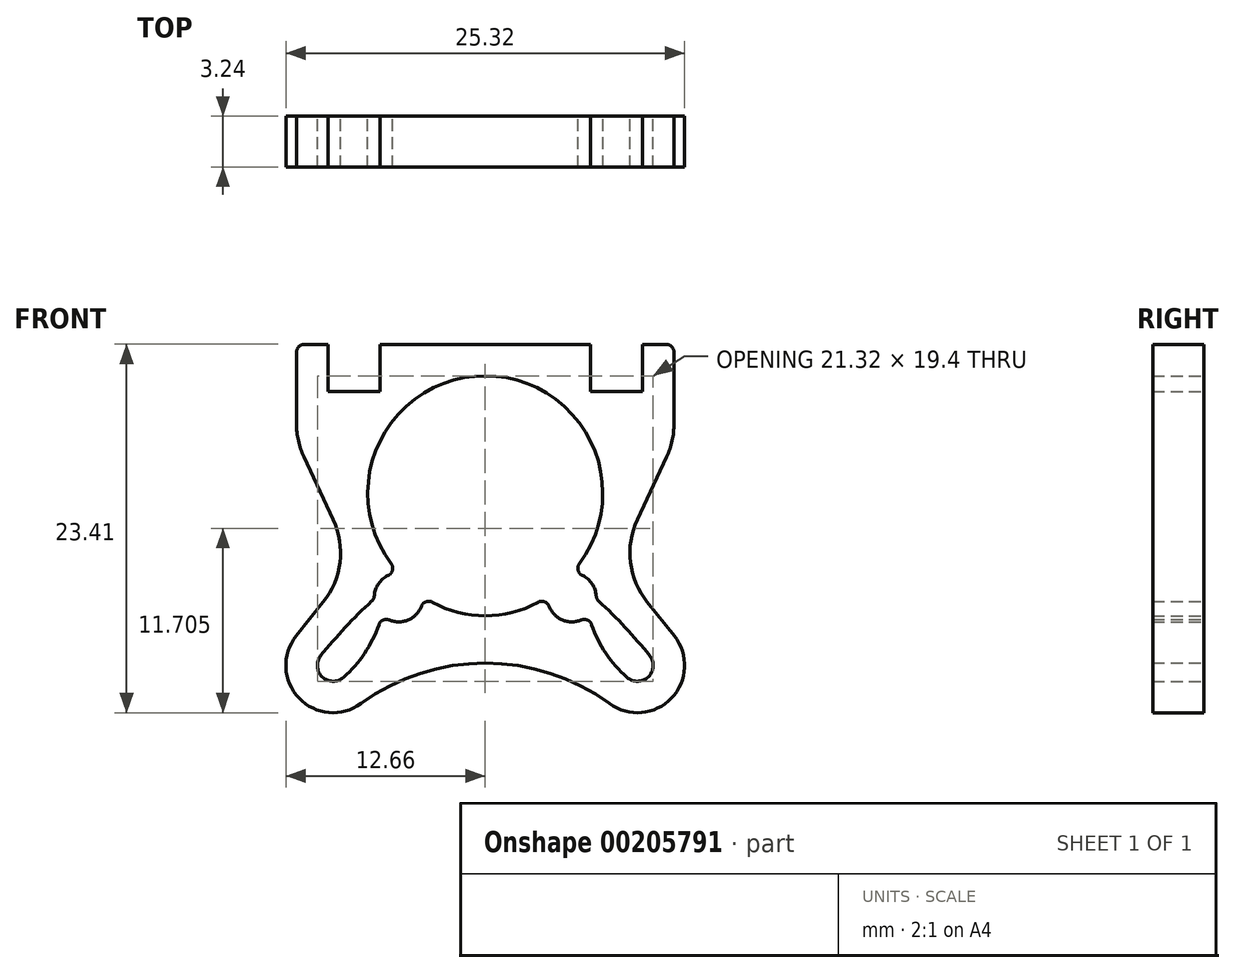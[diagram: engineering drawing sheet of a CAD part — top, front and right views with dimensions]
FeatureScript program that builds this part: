
annotation { "Feature Type Name" : "Feature", "Feature Type Description" : "" }
export const myFeature = defineFeature(function(context is Context, id is Id, definition is map)
    precondition{}
    {
        {
            var Q0;
            Q0=qCreatedBy(makeId("Front.planeOp"),FACE);
            var sketch = newSketch(context, id + "F0", { "sketchPlane" : qUnion([Q0])});
            skCircle(sketch, "E0", {"center": v(0, 0) * mm, "radius": 6.38 * mm});
            skPoint(sketch, "E1", {"position": v(0, 6.38) * mm});
            skPoint(sketch, "E2", {"position": v(0, 11.38) * mm});
            skCircle(sketch, "E3", {"center": v(-5.5, -5.7) * mm, "radius": 1.55 * mm});
            skLineSegment(sketch, "E4", {"start": v(0, 11.38) * mm, "end": v(0, 0) * mm, "construction": true});
            skCircle(sketch, "E5.MirrorC", {"center": v(5.5, -5.7) * mm, "radius": 1.55 * mm});
            skLineSegment(sketch, "E6", {"start": v(-5.5, -5.7) * mm, "end": v(5.5, -5.7) * mm, "construction": true});
            skSolve(sketch);
        }
        {
            var Q0;
            Q0=qCreatedBy(makeId("Front.planeOp"),FACE);
            var sketch = newSketch(context, id + "F1", { "sketchPlane" : qUnion([Q0])});
            skArc(sketch, "E7.0", {"start": v(-3.95, -5.63) * mm, "mid": v(-2.07, -6.56) * mm, "end": v(0, -6.88) * mm});
            skArc(sketch, "E8.3", {"start": v(-6.58, -6.82) * mm, "mid": v(-4.86, -7.12) * mm, "end": v(-3.95, -5.63) * mm});
            skLineSegment(sketch, "E9", {"start": v(0, 0) * mm, "end": v(-9.66, -10.03) * mm, "construction": true});
            skArc(sketch, "E10", {"start": v(-10.44, -9.4) * mm, "mid": v(-10.36, -10.75) * mm, "end": v(-9, -10.78) * mm});
            skLineSegment(sketch, "E11", {"start": v(-5.48, -4.16) * mm, "end": v(-7.05, -5.79) * mm, "construction": true});
            skLineSegment(sketch, "E12", {"start": v(-3.95, -5.63) * mm, "end": v(-5.52, -7.26) * mm, "construction": true});
            skLineSegment(sketch, "E13", {"start": v(-9, -10.78) * mm, "end": v(-4.74, -7.06) * mm, "construction": true});
            skPoint(sketch, "E13.endSnap0", {"position": v(-4.74, -6.44) * mm});
            skLineSegment(sketch, "E14", {"start": v(-6.7, -4.74) * mm, "end": v(-10.44, -9.4) * mm, "construction": true});
            skArc(sketch, "E15.trimOffspring", {"start": v(-12, -8.15) * mm, "mid": v(-11.83, -12.1) * mm, "end": v(-7.9, -12.45) * mm});
            skLineSegment(sketch, "E16", {"start": v(0, 0) * mm, "end": v(0, -9.88) * mm, "construction": true});
            skArc(sketch, "E17", {"start": v(0, -9.88) * mm, "mid": v(-4.15, -10.53) * mm, "end": v(-7.9, -12.45) * mm});
            skLineSegment(sketch, "E18", {"start": v(0, -9.88) * mm, "end": v(-5.5, -9.88) * mm, "construction": true});
            skLineSegment(sketch, "E19", {"start": v(0, -9.88) * mm, "end": v(0, -6.88) * mm});
            skArc(sketch, "E20", {"start": v(-5.48, -4.16) * mm, "mid": v(-6.62, -4.63) * mm, "end": v(-7.05, -5.79) * mm});
            skArc(sketch, "E21", {"start": v(-7.05, -5.79) * mm, "mid": v(-8.82, -7.53) * mm, "end": v(-10.44, -9.4) * mm});
            skLineSegment(sketch, "E22", {"start": v(-12, -8.15) * mm, "end": v(-8.33, -3.57) * mm});
            skArc(sketch, "E23", {"start": v(0, 8.37) * mm, "mid": v(-6.84, 3.9) * mm, "end": v(-5.48, -4.16) * mm});
            skLineSegment(sketch, "E24", {"start": v(0, 8.38) * mm, "end": v(0, 10.37) * mm});
            skLineSegment(sketch, "E25", {"start": v(-11.99, 4.22) * mm, "end": v(-8.57, -3.09) * mm});
            skArc(sketch, "E26.trimOffspring", {"start": v(-8.57, -3.09) * mm, "mid": v(-8.46, -3.33) * mm, "end": v(-8.33, -3.57) * mm});
            skArc(sketch, "E27", {"start": v(-9, -10.78) * mm, "mid": v(-7.49, -8.99) * mm, "end": v(-6.58, -6.82) * mm});
            skLineSegment(sketch, "E28", {"start": v(0, 10.37) * mm, "end": v(-6.69, 10.37) * mm});
            skLineSegment(sketch, "E29", {"start": v(-6.69, 10.37) * mm, "end": v(-6.69, 7.37) * mm});
            skLineSegment(sketch, "E30", {"start": v(-6.69, 7.37) * mm, "end": v(-9.99, 7.37) * mm});
            skLineSegment(sketch, "E31", {"start": v(-9.99, 7.37) * mm, "end": v(-9.99, 10.37) * mm});
            skLineSegment(sketch, "E32", {"start": v(-9.99, 10.37) * mm, "end": v(-11.99, 10.37) * mm});
            skLineSegment(sketch, "E33", {"start": v(-11.99, 10.37) * mm, "end": v(-11.99, 4.22) * mm});
            skLineSegment(sketch, "E34", {"start": v(-9.99, 10.37) * mm, "end": v(-9.99, 4.22) * mm, "construction": true});
            skLineSegment(sketch, "E35", {"start": v(-9.99, 4.22) * mm, "end": v(-6.69, 4.22) * mm, "construction": true});
            skLineSegment(sketch, "E36", {"start": v(-6.69, 4.22) * mm, "end": v(-6.69, 10.37) * mm, "construction": true});
            skLineSegment(sketch, "E37", {"start": v(-9.66, -13.03) * mm, "end": v(0, -13.03) * mm, "construction": true});
            skLineSegment(sketch, "E38", {"start": v(0, -13.03) * mm, "end": v(0, -6.88) * mm, "construction": true});
            skSolve(sketch);
        }
        {
            var Q0;
            Q0=qSketchRegion(id+"F1",true);
            extrude(context, id + "F2", {"entities" : qUnion([Q0]), "depth" : 3.25 * mm, "symmetric" : true});
        }
        {
            var Q0;
            Q0=makeQuery(id+"F2.opExtrude","SWEPT_EDGE",EDGE,{"disambiguationData":[OSD([sQuery(id+"F1.wireOp",EDGE,"E8.3"),sQuery(id+"F1.wireOp",EDGE,"f16a48b5-7a2a-4cbf-833e-9f4b7a7ec827.trimOffspring")])]});
            var Q1;
            Q1=makeQuery(id+"F2.opExtrude","SWEPT_EDGE",EDGE,{"disambiguationData":[OSD([sQuery(id+"F1.wireOp",EDGE,"0503ed2f-4905-41a0-8b90-6c5d83e06de4"),sQuery(id+"F1.wireOp",EDGE,"E8.3")])]});
            var Q2;
            Q2=makeQuery(id+"F2.opExtrude","SWEPT_EDGE",EDGE,{"disambiguationData":[OSD([sQuery(id+"F1.wireOp",EDGE,"E7.0"),sQuery(id+"F1.wireOp",EDGE,"E8.3")])]});
            var Q3;
            Q3=makeQuery(id+"F2.opExtrude","SWEPT_EDGE",EDGE,{"disambiguationData":[OSD([sQuery(id+"F1.wireOp",EDGE,"E20"),sQuery(id+"F1.wireOp",EDGE,"E21")])]});
            var Q4;
            Q4=makeQuery(id+"F2.opExtrude","SWEPT_EDGE",EDGE,{"disambiguationData":[OSD([sQuery(id+"F1.wireOp",EDGE,"E20"),sQuery(id+"F1.wireOp",EDGE,"aa0188ab-c223-4f96-b803-20454a8c8853")])]});
            var Q5;
            Q5=makeQuery(id+"F2.opExtrude","SWEPT_EDGE",EDGE,{"disambiguationData":[OSD([sQuery(id+"F1.wireOp",EDGE,"e83e305f-1027-4866-97f5-19716599f6f7"),sQuery(id+"F1.wireOp",EDGE,"E8.3")])]});
            var Q6;
            Q6=makeQuery(id+"F2.opExtrude","SWEPT_EDGE",EDGE,{"disambiguationData":[OSD([sQuery(id+"F1.wireOp",EDGE,"E10"),sQuery(id+"F1.wireOp",EDGE,"e83e305f-1027-4866-97f5-19716599f6f7")])]});
            var Q7;
            Q7=makeQuery(id+"F2.opExtrude","SWEPT_EDGE",EDGE,{"disambiguationData":[OSD([sQuery(id+"F1.wireOp",EDGE,"E32"),sQuery(id+"F1.wireOp",EDGE,"E33")])]});
            fillet(context, id + "F3", {"entities" : qUnion([Q0, Q1, Q2, Q3, Q4, Q5, Q6, Q7]), "radius" : 0.5 * mm, "tangentPropagation" : true, "allowEdgeOverflow" : false});
        }
        {
            var Q0;
            Q0=makeQuery(id+"F2.opExtrude","SWEPT_EDGE",EDGE,{"disambiguationData":[OSD([sQuery(id+"F1.wireOp",EDGE,"E22"),sQuery(id+"F1.wireOp",EDGE,"E26.trimOffspring")])]});
            var Q1;
            Q1=makeQuery(id+"F2.opExtrude","SWEPT_EDGE",EDGE,{"disambiguationData":[OSD([sQuery(id+"F1.wireOp",EDGE,"E25"),sQuery(id+"F1.wireOp",EDGE,"E33")])]});
            fillet(context, id + "F4", {"entities" : qUnion([Q0, Q1]), "radius" : 5 * mm, "tangentPropagation" : true, "allowEdgeOverflow" : false});
        }
        {
            var Q0;
            Q0=makeQuery(id+"F2.opExtrude","SWEPT_BODY",BODY,{"disambiguationData":[OSD([sQuery(id+"F1.wireOp",EDGE,"91029bab-c422-4aac-b43c-f8eb8f7441cb.0"),sQuery(id+"F1.wireOp",EDGE,"E7.0"),sQuery(id+"F1.wireOp",EDGE,"E8.0"),sQuery(id+"F1.wireOp",EDGE,"E8.3"),sQuery(id+"F1.wireOp",EDGE,"4fe737ca-cd33-4ae7-bfb5-aca6cdd2fbdd"),sQuery(id+"F1.wireOp",EDGE,"E10"),sQuery(id+"F1.wireOp",EDGE,"87521696-a49b-46d6-ae6d-b95a5258b794"),sQuery(id+"F1.wireOp",EDGE,"3ad451f8-88f0-40d6-b978-8860d0f46c41"),sQuery(id+"F1.wireOp",EDGE,"RmzYGLSE-aIne-cmcq-fouj-xsO9WjanKBXf"),sQuery(id+"F1.wireOp",EDGE,"E1ndacnS-k5oY-T1jz-uEtG-vA6wWoizQWTL"),sQuery(id+"F1.wireOp",EDGE,"290a5299-caae-4b93-a680-34ceb27d99b0"),sQuery(id+"F1.wireOp",EDGE,"acf9eb55-ab42-4665-aab6-df971979b8c6"),sQuery(id+"F1.wireOp",EDGE,"0503ed2f-4905-41a0-8b90-6c5d83e06de4"),sQuery(id+"F1.wireOp",EDGE,"e83e305f-1027-4866-97f5-19716599f6f7"),sQuery(id+"F1.wireOp",EDGE,"E8.3"),sQuery(id+"F1.wireOp",EDGE,"E15.trimOffspring"),sQuery(id+"F1.wireOp",EDGE,"140a15c2-b3ae-4d8c-875c-2f7ce67bd9a0.trimOffspring"),sQuery(id+"F1.wireOp",EDGE,"f16a48b5-7a2a-4cbf-833e-9f4b7a7ec827.trimOffspring"),sQuery(id+"F1.wireOp",EDGE,"c726c67e-1b0a-4414-994c-10f8da0a7d9b.trimOffspring"),sQuery(id+"F1.wireOp",EDGE,"E17"),sQuery(id+"F1.wireOp",EDGE,"9d4cf9fb-cccf-4056-9c7a-a0118e21bfc9.trimOffspring"),sQuery(id+"F1.wireOp",EDGE,"aw0qZEzT-GYTq-v6Y8-Owwz-bXgHvjQE39bA"),sQuery(id+"F1.wireOp",EDGE,"E19"),sQuery(id+"F1.wireOp",EDGE,"e7ad43b5-d072-4a5a-872d-9ebe676b2ed9.trimOffspring")])]});
            var Q1;
            Q1=qCreatedBy(makeId("Right.planeOp"),FACE);
            mirror(context, id + "F5", {"operationType" : NewBodyOperationType.ADD, "entities" : qUnion([Q0]), "mirrorPlane" : qUnion([Q1])});
        }
    });
